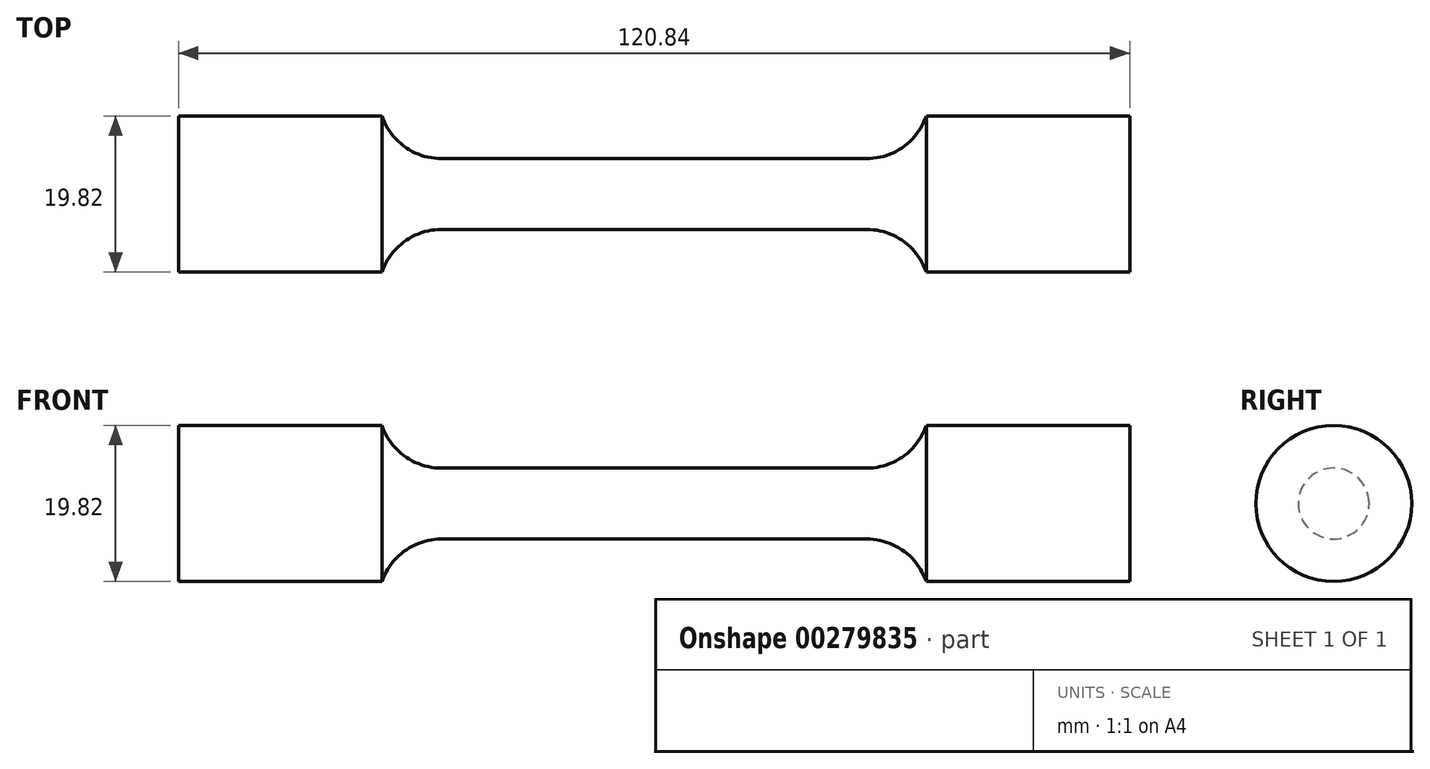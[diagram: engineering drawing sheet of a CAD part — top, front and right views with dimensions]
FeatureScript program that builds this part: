
annotation { "Feature Type Name" : "Feature", "Feature Type Description" : "" }
export const myFeature = defineFeature(function(context is Context, id is Id, definition is map)
    precondition{}
    {
        {
            var Q0;
            Q0=qCreatedBy(makeId("Front.planeOp"),FACE);
            var sketch = newSketch(context, id + "F0", { "sketchPlane" : qUnion([Q0])});
            skLineSegment(sketch, "E0", {"start": v(0, 4.5) * mm, "end": v(27, 4.5) * mm});
            skArc(sketch, "E1", {"start": v(27, 4.5) * mm, "mid": v(31.65, 6) * mm, "end": v(34.57, 9.9) * mm});
            skLineSegment(sketch, "E2", {"start": v(34.57, 9.9) * mm, "end": v(60.42, 9.9) * mm});
            skLineSegment(sketch, "E3", {"start": v(60.42, 9.9) * mm, "end": v(60.42, 0) * mm});
            skLineSegment(sketch, "E4.MirrorCS", {"start": v(0, 4.5) * mm, "end": v(-27, 4.5) * mm});
            skLineSegment(sketch, "E5.MirrorCS", {"start": v(-34.57, 9.9) * mm, "end": v(-60.42, 9.9) * mm});
            skArc(sketch, "E6.MirrorCS", {"start": v(-27, 4.5) * mm, "mid": v(-31.65, 6) * mm, "end": v(-34.57, 9.9) * mm});
            skLineSegment(sketch, "E7.MirrorCS", {"start": v(-60.42, 9.9) * mm, "end": v(-60.42, 0) * mm});
            skLineSegment(sketch, "E8", {"start": v(-60.42, 0) * mm, "end": v(60.42, 0) * mm});
            skSolve(sketch);
        }
        {
            var Q0;
            Q0=makeQuery(id+"F0.imprint","IMPRINT",FACE,{"disambiguationData":[TD([[makeQuery(id+"F0.imprint","IMPRINT",EDGE,{"derivedFrom":sQuery(id+"F0.wireOp",EDGE,"E0")}),-1.0]])]});
            var Q1;
            Q1=sQuery(id+"F0.wireOp",EDGE,"E8");
            revolve(context, id + "F1", {"entities" : qUnion([Q0]), "axis" : qUnion([Q1]), "revolveType" : RevolveType.FULL});
        }
    });
